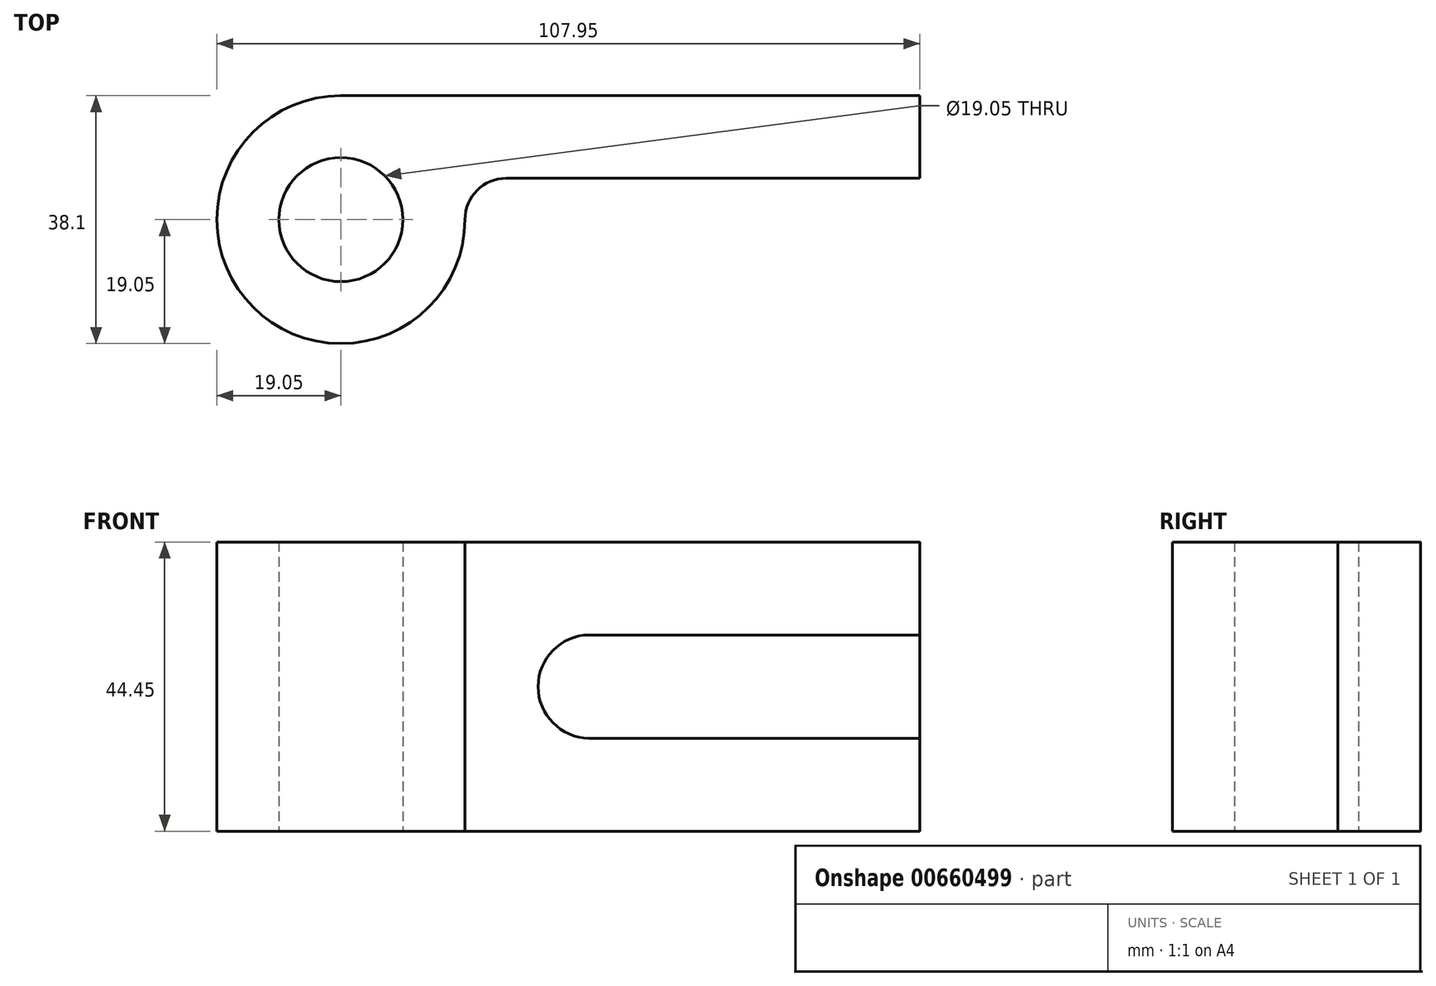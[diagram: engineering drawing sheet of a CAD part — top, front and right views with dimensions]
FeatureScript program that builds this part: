
annotation { "Feature Type Name" : "Feature", "Feature Type Description" : "" }
export const myFeature = defineFeature(function(context is Context, id is Id, definition is map)
    precondition{}
    {
        {
            var Q0;
            Q0=qCreatedBy(makeId("Top.planeOp"),FACE);
            var sketch = newSketch(context, id + "F0", { "sketchPlane" : qUnion([Q0])});
            skCircle(sketch, "E0", {"center": v(0, 0) * mm, "radius": 9.53 * mm});
            skCircle(sketch, "E1", {"center": v(0, 0) * mm, "radius": 19.05 * mm});
            skLineSegment(sketch, "E2", {"start": v(0, 19.05) * mm, "end": v(88.9, 19.05) * mm});
            skLineSegment(sketch, "E3", {"start": v(88.9, 19.05) * mm, "end": v(88.9, 6.35) * mm});
            skLineSegment(sketch, "E4", {"start": v(88.9, 6.35) * mm, "end": v(17.96, 6.35) * mm});
            skSolve(sketch);
        }
        {
            var Q0;
            Q0=makeQuery(id+"F0.imprint","IMPRINT",FACE,{"disambiguationData":[TD([[makeQuery(id+"F0.imprint","IMPRINT",EDGE,{"derivedFrom":sQuery(id+"F0.wireOp",EDGE,"E0")}),-1.0]])]});
            var Q1;
            {var subQ0=sQuery(id+"F0.wireOp",EDGE,"E2");Q1=makeQuery(id+"F0.imprint","IMPRINT",FACE,{"disambiguationData":[TD([[makeQuery(id+"F0.imprint","IMPRINT",EDGE,{"derivedFrom":subQ0}),-1.0]])]});}
            extrude(context, id + "F1", {"entities" : qUnion([Q0, Q1]), "depth" : 44.45 * mm, "offsetDistance" : 25.4 * mm});
        }
        {
            var Q0;
            Q0=makeQuery(id+"F1.opExtrude","SWEPT_FACE",FACE,{"disambiguationData":[OSD([sQuery(id+"F0.wireOp",EDGE,"E4")])]});
            var sketch = newSketch(context, id + "F2", { "sketchPlane" : qUnion([Q0])});
            skLineSegment(sketch, "E5.bottom", {"start": v(88.9, 30.16) * mm, "end": v(38.1, 30.16) * mm});
            skLineSegment(sketch, "E5.top", {"start": v(88.9, 14.29) * mm, "end": v(38.1, 14.29) * mm});
            skLineSegment(sketch, "E5.left", {"start": v(88.9, 30.16) * mm, "end": v(88.9, 14.29) * mm});
            skLineSegment(sketch, "E5.right", {"start": v(38.1, 30.16) * mm, "end": v(38.1, 14.29) * mm});
            skSolve(sketch);
        }
        {
            var Q0;
            {var subQ2=sQuery(id+"F2.wireOp",EDGE,"E5.bottom");Q0=makeQuery(id+"F2.imprint","IMPRINT",FACE,{"disambiguationData":[TD([[makeQuery(id+"F2.imprint","IMPRINT",EDGE,{"derivedFrom":subQ2}),-1.0]])]});}
            var sketch = newSketch(context, id + "F3", { "sketchPlane" : qUnion([Q0])});
            skCircle(sketch, "E6", {"center": v(38.22, 22.22) * mm, "radius": 7.94 * mm});
            skSolve(sketch);
        }
        {
            var Q0;
            {var subQ0=sQuery(id+"F3.wireOp",EDGE,"E6");var subQ1=makeQuery(id+"F2.imprint","IMPRINT",EDGE,{"derivedFrom":sQuery(id+"F2.wireOp",EDGE,"E5.right")});var subQ2=makeQuery(id+"F3.imprint","INTERSECT",VERTEX,{"disambiguationData":[OD(0.0)],"derivedFrom":[subQ1,subQ0]});Q0=makeQuery(id+"F3.imprint","IMPRINT",FACE,{"disambiguationData":[TD([[makeQuery(id+"F3.imprint","IMPRINT",EDGE,{"disambiguationData":[TD([[subQ2,-1.0]])],"derivedFrom":subQ0}),1.0]])]});}
            var Q1;
            Q1=makeQuery(id+"F2.imprint","IMPRINT",FACE,{"disambiguationData":[TD([[makeQuery(id+"F2.imprint","IMPRINT",EDGE,{"derivedFrom":sQuery(id+"F2.wireOp",EDGE,"E5.bottom")}),1.0]])]});
            extrude(context, id + "F4", {"entities" : qUnion([Q0, Q1]), "operationType" : NewBodyOperationType.REMOVE, "oppositeDirection" : true, "depth" : 1 / 50.8 * mm, "offsetDistance" : 25.4 * mm});
        }
        {
            var Q0;
            Q0=makeQuery(id+"F1.opExtrude","CAP_EDGE",EDGE,{"disambiguationData":[OSD([sQuery(id+"F0.wireOp",EDGE,"E3")])],"isStart":false});
            var Q1;
            Q1=makeQuery(id+"F1.opExtrude","CAP_EDGE",EDGE,{"disambiguationData":[OSD([sQuery(id+"F0.wireOp",EDGE,"E3")])],"isStart":true});
            fillet(context, id + "F5", {"entities" : qUnion([Q0, Q1]), "radius" : 3 / 203.2 * mm, "tangentPropagation" : true, "allowEdgeOverflow" : false});
        }
        {
            var Q0;
            Q0=makeQuery(id+"F1.opExtrude","SWEPT_EDGE",EDGE,{"disambiguationData":[OSD([sQuery(id+"F0.wireOp",EDGE,"E1"),sQuery(id+"F0.wireOp",EDGE,"E4")])]});
            fillet(context, id + "F6", {"entities" : qUnion([Q0]), "radius" : 6.35 * mm, "tangentPropagation" : true, "allowEdgeOverflow" : false});
        }
    });
